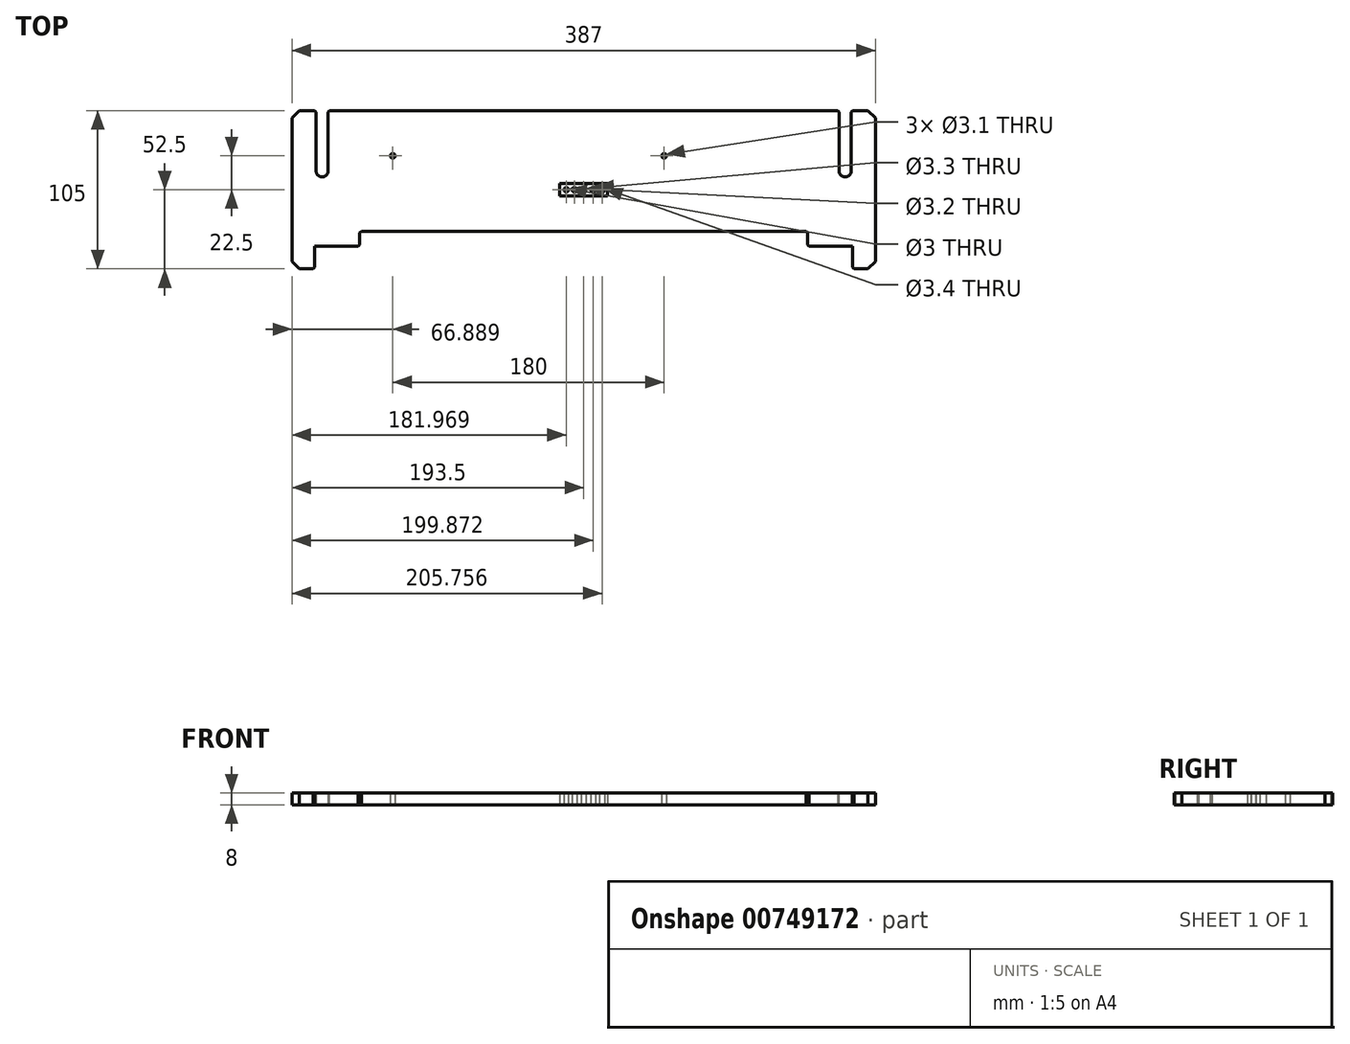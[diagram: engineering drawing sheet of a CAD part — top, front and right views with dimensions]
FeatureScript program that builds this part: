
annotation { "Feature Type Name" : "Feature", "Feature Type Description" : "" }
export const myFeature = defineFeature(function(context is Context, id is Id, definition is map)
    precondition{}
    {
        {
            var Q0;
            Q0=qCreatedBy(makeId("Top.planeOp"),FACE);
            var sketch = newSketch(context, id + "F0", { "sketchPlane" : qUnion([Q0])});
            skLineSegment(sketch, "E0.bottom", {"start": v(193.5, 52.5) * mm, "end": v(-193.5, 52.5) * mm});
            skLineSegment(sketch, "E0.top", {"start": v(193.5, -52.5) * mm, "end": v(178.5, -52.5) * mm});
            skLineSegment(sketch, "E0.left", {"start": v(193.5, 52.5) * mm, "end": v(193.5, -52.5) * mm});
            skLineSegment(sketch, "E0.right", {"start": v(-193.5, 52.5) * mm, "end": v(-193.5, -52.5) * mm});
            skPoint(sketch, "E0.middle", {"position": v(0, 0) * mm});
            skLineSegment(sketch, "E1.top", {"start": v(178.5, -37.5) * mm, "end": v(-178.5, -37.5) * mm});
            skLineSegment(sketch, "E1.left", {"start": v(178.5, -52.5) * mm, "end": v(178.5, -37.5) * mm});
            skLineSegment(sketch, "E1.right", {"start": v(-178.5, -52.5) * mm, "end": v(-178.5, -37.5) * mm});
            skPoint(sketch, "E1.middle", {"position": v(0, -45) * mm});
            skLineSegment(sketch, "E2.trimOffspring", {"start": v(-178.5, -52.5) * mm, "end": v(-193.5, -52.5) * mm});
            skPoint(sketch, "E3", {"position": v(0, -40) * mm});
            skLineSegment(sketch, "E4", {"start": v(-126.61, 22.5) * mm, "end": v(53.39, 22.5) * mm, "construction": true});
            skCircle(sketch, "E5", {"center": v(53.39, 22.5) * mm, "radius": 1.55 * mm});
            skCircle(sketch, "E6", {"center": v(-126.61, 22.5) * mm, "radius": 1.55 * mm});
            skArc(sketch, "E7", {"start": v(-121.61, 52.5) * mm, "mid": v(-146.61, 27.5) * mm, "end": v(-121.61, 2.5) * mm, "construction": true});
            skArc(sketch, "E8", {"start": v(88.39, 52.5) * mm, "mid": v(113.39, 27.5) * mm, "end": v(88.39, 2.5) * mm, "construction": true});
            skLineSegment(sketch, "E9", {"start": v(-121.61, 52.5) * mm, "end": v(88.39, 52.5) * mm, "construction": true});
            skLineSegment(sketch, "E10", {"start": v(88.39, 2.5) * mm, "end": v(-121.61, 2.5) * mm, "construction": true});
            skPoint(sketch, "E11", {"position": v(-146.61, 27.5) * mm});
            skPoint(sketch, "E12", {"position": v(113.39, 27.5) * mm});
            skCircle(sketch, "E13", {"center": v(-173.5, 12.5) * mm, "radius": 4 * mm});
            skCircle(sketch, "E14", {"center": v(173.5, 12.5) * mm, "radius": 4 * mm});
            skLineSegment(sketch, "E15", {"start": v(-177.5, 12.5) * mm, "end": v(-177.5, 52.5) * mm});
            skLineSegment(sketch, "E16", {"start": v(-169.5, 12.5) * mm, "end": v(-169.5, 52.5) * mm});
            skLineSegment(sketch, "E17", {"start": v(169.5, 12.5) * mm, "end": v(169.5, 52.5) * mm});
            skLineSegment(sketch, "E18", {"start": v(177.5, 12.5) * mm, "end": v(177.5, 52.5) * mm});
            skLineSegment(sketch, "E19", {"start": v(-173.5, 12.5) * mm, "end": v(173.5, 12.5) * mm, "construction": true});
            skPoint(sketch, "E20", {"position": v(0, 12.5) * mm});
            skLineSegment(sketch, "E21.bottom", {"start": v(148.5, -37.5) * mm, "end": v(-148.5, -37.5) * mm});
            skLineSegment(sketch, "E21.top", {"start": v(148.5, -27.5) * mm, "end": v(-148.5, -27.5) * mm});
            skLineSegment(sketch, "E21.left", {"start": v(148.5, -37.5) * mm, "end": v(148.5, -27.5) * mm});
            skLineSegment(sketch, "E21.right", {"start": v(-148.5, -37.5) * mm, "end": v(-148.5, -27.5) * mm});
            skPoint(sketch, "E21.middle", {"position": v(0, -32.5) * mm});
            skSolve(sketch);
        }
        {
            var Q0;
            Q0=makeQuery(id+"F0.imprint","IMPRINT",FACE,{"disambiguationData":[TD([[makeQuery(id+"F0.imprint","IMPRINT",EDGE,{"derivedFrom":sQuery(id+"F0.wireOp",EDGE,"E0.top")}),-1.0]])]});
            extrude(context, id + "F1", {"entities" : qUnion([Q0]), "depth" : 8 * mm, "offsetDistance" : 25 * mm});
        }
        {
            var Q0;
            Q0=makeQuery(id+"F1.opExtrude","SWEPT_EDGE",EDGE,{"disambiguationData":[OSD([sQuery(id+"F0.wireOp",EDGE,"E0.bottom"),sQuery(id+"F0.wireOp",EDGE,"E0.right")])]});
            var Q1;
            Q1=makeQuery(id+"F1.opExtrude","SWEPT_EDGE",EDGE,{"disambiguationData":[OSD([sQuery(id+"F0.wireOp",EDGE,"E0.right"),sQuery(id+"F0.wireOp",EDGE,"E2.trimOffspring")])]});
            var Q2;
            Q2=makeQuery(id+"F1.opExtrude","SWEPT_EDGE",EDGE,{"disambiguationData":[OSD([sQuery(id+"F0.wireOp",EDGE,"E0.top"),sQuery(id+"F0.wireOp",EDGE,"E0.left")])]});
            var Q3;
            Q3=makeQuery(id+"F1.opExtrude","SWEPT_EDGE",EDGE,{"disambiguationData":[OSD([sQuery(id+"F0.wireOp",EDGE,"E0.bottom"),sQuery(id+"F0.wireOp",EDGE,"E0.left")])]});
            chamfer(context, id + "F2", {"entities" : qUnion([Q0, Q1, Q2, Q3]), "width" : 5 * mm, "tangentPropagation" : true});
        }
        {
            var Q0;
            Q0=qCreatedBy(makeId("Top.planeOp"),FACE);
            var sketch = newSketch(context, id + "F3", { "sketchPlane" : qUnion([Q0])});
            skLineSegment(sketch, "E22.bottom", {"start": v(-15.96, -4.14) * mm, "end": v(15.96, -4.14) * mm});
            skLineSegment(sketch, "E22.top", {"start": v(-15.96, 4.14) * mm, "end": v(15.96, 4.14) * mm});
            skLineSegment(sketch, "E22.left", {"start": v(-15.96, -4.14) * mm, "end": v(-15.96, 4.14) * mm});
            skLineSegment(sketch, "E22.right", {"start": v(15.96, -4.14) * mm, "end": v(15.96, 4.14) * mm});
            skPoint(sketch, "E22.middle", {"position": v(0, 0) * mm});
            skCircle(sketch, "E23", {"center": v(-11.53, 0) * mm, "radius": 1.5 * mm});
            skCircle(sketch, "E24", {"center": v(-6.1, 0) * mm, "radius": 1.55 * mm});
            skCircle(sketch, "E25", {"center": v(0, 0) * mm, "radius": 1.6 * mm});
            skCircle(sketch, "E26", {"center": v(6.37, 0) * mm, "radius": 1.65 * mm});
            skCircle(sketch, "E27", {"center": v(12.26, 0) * mm, "radius": 1.7 * mm});
            skSolve(sketch);
        }
        {
            var Q0;
            Q0=makeQuery(id+"F3.imprint","IMPRINT",FACE,{"disambiguationData":[TD([[makeQuery(id+"F3.imprint","IMPRINT",EDGE,{"derivedFrom":sQuery(id+"F3.wireOp",EDGE,"E22.bottom")}),1.0]])]});
            extrude(context, id + "F4", {"entities" : qUnion([Q0]), "depth" : 8 * mm, "offsetDistance" : 25 * mm});
        }
        {
            var Q0;
            Q0=makeQuery(id+"F1.opExtrude","SWEPT_EDGE",EDGE,{"disambiguationData":[OSD([sQuery(id+"F0.wireOp",EDGE,"E1.right"),sQuery(id+"F0.wireOp",EDGE,"E2.trimOffspring")])]});
            var Q1;
            Q1=makeQuery(id+"F1.opExtrude","SWEPT_EDGE",EDGE,{"disambiguationData":[OSD([sQuery(id+"F0.wireOp",EDGE,"E0.top"),sQuery(id+"F0.wireOp",EDGE,"E1.left")])]});
            var Q2;
            Q2=makeQuery(id+"F1.opExtrude","SWEPT_EDGE",EDGE,{"disambiguationData":[OSD([sQuery(id+"F0.wireOp",EDGE,"E0.bottom"),sQuery(id+"F0.wireOp",EDGE,"E18")])]});
            var Q3;
            Q3=makeQuery(id+"F1.opExtrude","SWEPT_EDGE",EDGE,{"disambiguationData":[OSD([sQuery(id+"F0.wireOp",EDGE,"E0.bottom"),sQuery(id+"F0.wireOp",EDGE,"E17")])]});
            var Q4;
            Q4=makeQuery(id+"F1.opExtrude","SWEPT_EDGE",EDGE,{"disambiguationData":[OSD([sQuery(id+"F0.wireOp",EDGE,"E0.bottom"),sQuery(id+"F0.wireOp",EDGE,"E15")])]});
            var Q5;
            Q5=makeQuery(id+"F1.opExtrude","SWEPT_EDGE",EDGE,{"disambiguationData":[OSD([sQuery(id+"F0.wireOp",EDGE,"E0.bottom"),sQuery(id+"F0.wireOp",EDGE,"E16")])]});
            var Q6;
            Q6=makeQuery(id+"F1.opExtrude","SWEPT_EDGE",EDGE,{"disambiguationData":[OSD([sQuery(id+"F0.wireOp",EDGE,"E21.top"),sQuery(id+"F0.wireOp",EDGE,"E21.right")])]});
            var Q7;
            Q7=makeQuery(id+"F1.opExtrude","SWEPT_EDGE",EDGE,{"disambiguationData":[OSD([sQuery(id+"F0.wireOp",EDGE,"E21.top"),sQuery(id+"F0.wireOp",EDGE,"E21.left")])]});
            var Q8;
            Q8=makeQuery(id+"F1.opExtrude","SWEPT_EDGE",EDGE,{"disambiguationData":[OSD([sQuery(id+"F0.wireOp",EDGE,"E1.top"),sQuery(id+"F0.wireOp",EDGE,"E21.bottom"),sQuery(id+"F0.wireOp",EDGE,"E21.left")])]});
            var Q9;
            Q9=makeQuery(id+"F1.opExtrude","SWEPT_EDGE",EDGE,{"disambiguationData":[OSD([sQuery(id+"F0.wireOp",EDGE,"E1.top"),sQuery(id+"F0.wireOp",EDGE,"E21.bottom"),sQuery(id+"F0.wireOp",EDGE,"E21.right")])]});
            chamfer(context, id + "F5", {"entities" : qUnion([Q0, Q1, Q2, Q3, Q4, Q5, Q6, Q7, Q8, Q9]), "width" : 1 * mm, "tangentPropagation" : true});
        }
    });
